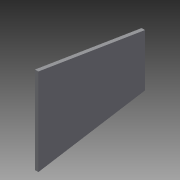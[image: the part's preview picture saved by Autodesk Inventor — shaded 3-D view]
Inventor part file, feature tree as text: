
AUTODESK INVENTOR PART (.ipt)
format: ipt  version: 2015 (Build 190159000, 159)  size: 102,400 bytes
history: native  units: in
note: dims shown in document units (in); Inventor stores cm internally (conversion verified against a paired STEP export)
features: extrude x3, sketch x3, projected_geometry x2
ambient origin geometry x8: Origin, YZ Plane, XZ Plane, XY Plane, X Axis, Y Axis, Z Axis, Center Point
bodies: Solid1 (feature_tree)
feature tree (8):
  extrude  "Extrusion1"  Depth=0.1969in TaperAngle=0.0deg
  extrude  "Extrusion2"  Depth=3.5in
  extrude  "Extrusion3"  Depth=1.5in
  sketch  "Sketch3"  dims[d0=10.0in d1=0.1969in d2=0.0in]
  sketch  "Sketch4"  dims[d3=3.5in d4=3.5in]
  projected_geometry  "Projected Loop1"
  sketch  "Sketch7"  dims[d5=2.5in d7=2.5in d8=0.1969in d9=0.0in d10=6.1241in d14=0.1969in d15=0.1969in d16=1.5in d17=0.0in]
  projected_geometry  "Projected Loop2"
